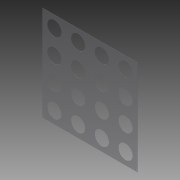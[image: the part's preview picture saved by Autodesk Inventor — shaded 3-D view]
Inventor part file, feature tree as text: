
AUTODESK INVENTOR PART (.ipt)
format: ipt  version: 2014 (Build 180170000, 170)  size: 181,248 bytes
history: native  units: in
note: dims shown in document units (in); Inventor stores cm internally (conversion verified against a paired STEP export)
features: extrude x3, sketch x3, pattern_linear x1
ambient origin geometry x8: Origin, YZ Plane, XZ Plane, XY Plane, X Axis, Y Axis, Z Axis, Center Point
bodies: Body1 (feature_tree)
feature tree (7):
  extrude  "Extrusion1"  Depth=20.0in
  extrude  "Extrusion3"  Depth=0.0312in
  pattern_linear  "Rectangular Pattern1"  Spacing1=2.5in  [1 undecoded]
  extrude  "Extrusion4"  Depth=2.5in
  sketch  "Sketch1"  dims[d5=20.0in d6=20.0in]
  sketch  "Sketch3"  dims[d10=0.0312in d11=0.0in d12=1.0in]
  sketch  "Sketch4"  dims[d26=3.0in d27=2.5in d28=2.5in d29=0.0625in d30=0.0in d31=1.5748in d33=5.0in d34=1.5748in d36=5.0in d67=0.196in d69=0.25in d70=0.25in d106=0.196in d107=0.7874in d109=0.5in d110=0.7874in d112=0.5in d115=0.25in d116=4.0in d117=0.75in d118=3.0in d119=0.196in d120=0.5in d121=0.25in d123=0.25in d124=1.0in d125=0.5in d126=0.196in d127=0.25in d128=1.0in d129=0.0in d130=2.0in d131=0.25in]
note: 1 required parameter value undecoded (feature->parameter linkage not recoverable at this tier; creation-order binding heuristic only, values carry confidence <= 0.55)
